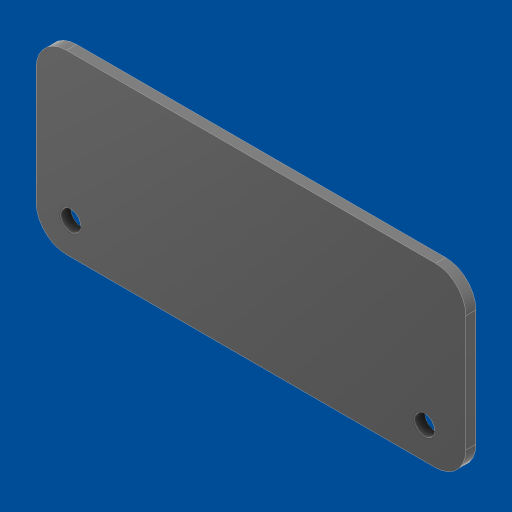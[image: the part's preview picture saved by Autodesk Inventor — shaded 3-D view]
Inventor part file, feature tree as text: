
AUTODESK INVENTOR PART (.ipt)
format: ipt  version: 2023.2 (Build 272271000, 271)  size: 121,856 bytes
history: native  units: mm
features: extrude x2, sketch x2
ambient origin geometry x8: Origin, YZ Plane, XZ Plane, XY Plane, X Axis, Y Axis, Z Axis, Center Point
bodies: Solid1 (feature_tree)
feature tree (4):
  extrude  "Extrusion1"  Depth=35.0mm
  extrude  "Extrusion2"  Depth=2.0mm
  sketch  "Sketch1"  dims[d0=2.0mm d1=0.0mm d2=35.0mm]
  sketch  "Sketch2"  dims[d3=11.0mm d4=70.0mm d5=4.0mm d6=4.0mm d7=4.0mm d8=4.0mm d9=2.0mm d10=2.0mm d11=0.0mm]
